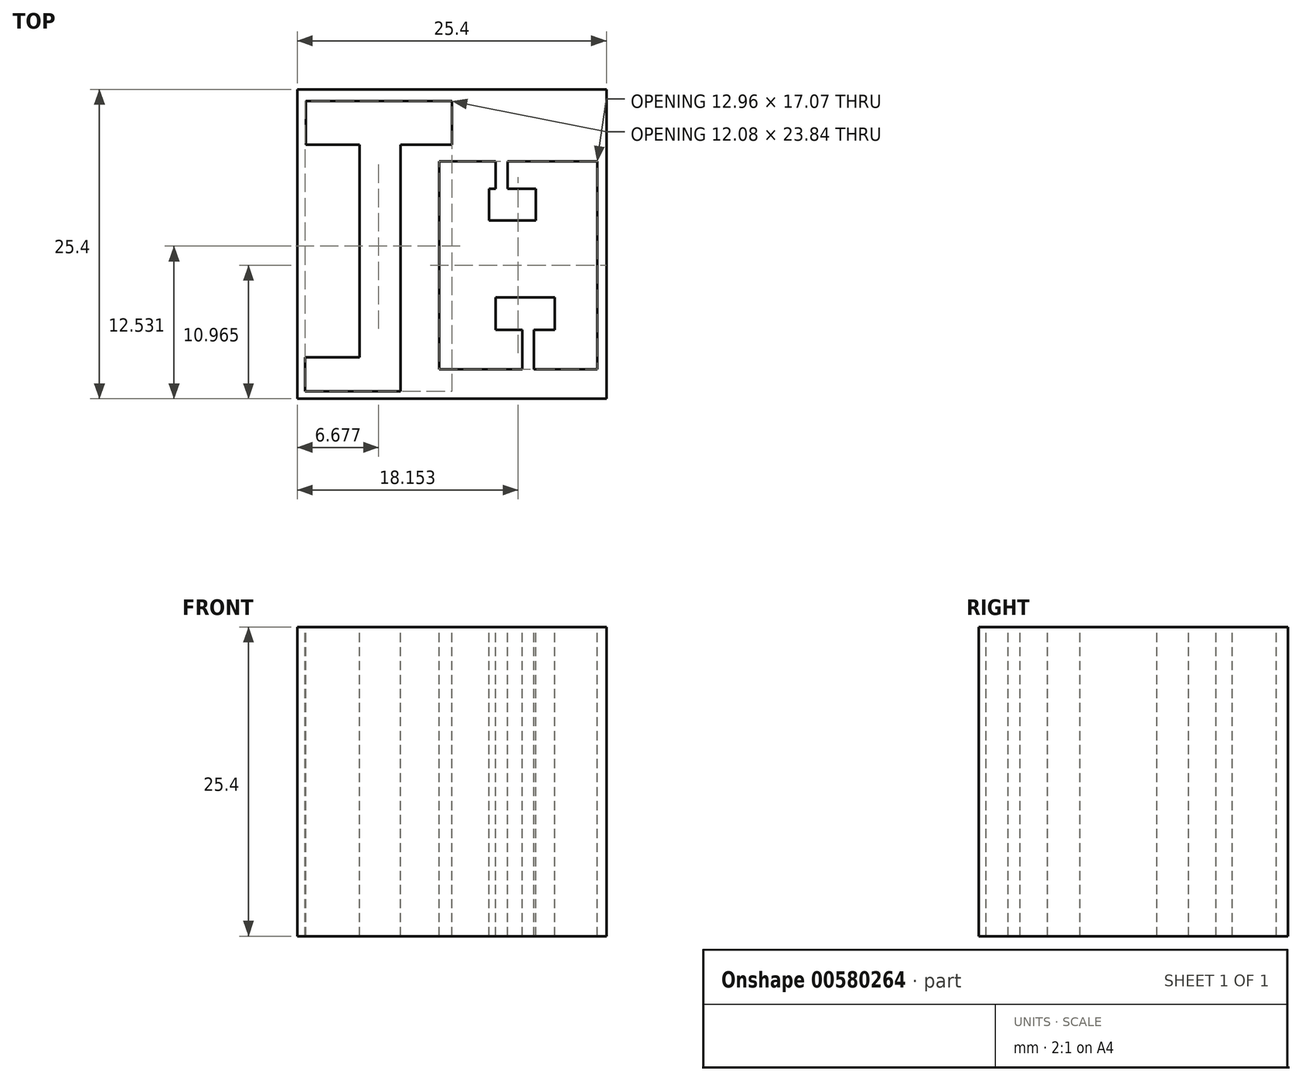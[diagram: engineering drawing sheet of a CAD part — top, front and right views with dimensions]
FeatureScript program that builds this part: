
annotation { "Feature Type Name" : "Feature", "Feature Type Description" : "" }
export const myFeature = defineFeature(function(context is Context, id is Id, definition is map)
    precondition{}
    {
        {
            var Q0;
            Q0=qCreatedBy(makeId("Top.planeOp"),FACE);
            var sketch = newSketch(context, id + "F0", { "sketchPlane" : qUnion([Q0])});
            skLineSegment(sketch, "E0.bottom", {"start": v(-13.3, 15.18) * mm, "end": v(12.1, 15.18) * mm});
            skLineSegment(sketch, "E0.top", {"start": v(-13.3, -10.22) * mm, "end": v(12.1, -10.22) * mm});
            skLineSegment(sketch, "E0.left", {"start": v(-13.3, 15.18) * mm, "end": v(-13.3, -10.22) * mm});
            skLineSegment(sketch, "E0.right", {"start": v(12.1, 15.18) * mm, "end": v(12.1, -10.22) * mm});
            skSolve(sketch);
        }
        {
            var Q0;
            Q0 = qSketchRegion(id + "F0", true);
            extrude(context, id + "F1", {"entities" : qUnion([Q0]), "depth" : 25.4 * mm, "offsetDistance" : 25.4 * mm});
        }
        {
            var Q0;
            Q0=makeQuery(id+"F1.opExtrude","CAP_FACE",FACE,{"disambiguationData":[OSD([sQuery(id+"F0.wireOp",EDGE,"E0.bottom"),sQuery(id+"F0.wireOp",EDGE,"E0.top"),sQuery(id+"F0.wireOp",EDGE,"E0.left"),sQuery(id+"F0.wireOp",EDGE,"E0.right")])],"isStart":false});
            var sketch = newSketch(context, id + "F2", { "sketchPlane" : qUnion([Q0])});
            skLineSegment(sketch, "E1.bottom", {"start": v(-12.6, 14.23) * mm, "end": v(-0.58, 14.23) * mm});
            skLineSegment(sketch, "E1.top", {"start": v(-12.6, 10.63) * mm, "end": v(-0.58, 10.63) * mm});
            skLineSegment(sketch, "E1.left", {"start": v(-12.6, 14.23) * mm, "end": v(-12.6, 10.63) * mm});
            skLineSegment(sketch, "E1.right", {"start": v(-0.58, 14.23) * mm, "end": v(-0.58, 10.63) * mm});
            skSolve(sketch);
        }
        {
            var Q0;
            Q0 = qSketchRegion(id + "F2", true);
            extrude(context, id + "F3", {"entities" : qUnion([Q0]), "operationType" : NewBodyOperationType.REMOVE, "endBound" : BoundingType.THROUGH_ALL, "oppositeDirection" : true, "depth" : 25.4 * mm, "offsetDistance" : 25.4 * mm});
        }
        {
            var Q0;
            Q0=makeQuery(id+"F1.opExtrude","CAP_FACE",FACE,{"disambiguationData":[OSD([sQuery(id+"F0.wireOp",EDGE,"E0.bottom"),sQuery(id+"F0.wireOp",EDGE,"E0.top"),sQuery(id+"F0.wireOp",EDGE,"E0.left"),sQuery(id+"F0.wireOp",EDGE,"E0.right")])],"isStart":false});
            var sketch = newSketch(context, id + "F4", { "sketchPlane" : qUnion([Q0])});
            skLineSegment(sketch, "E2.bottom", {"start": v(-8.17, 10.63) * mm, "end": v(-4.82, 10.63) * mm});
            skLineSegment(sketch, "E2.top", {"start": v(-8.17, -6.83) * mm, "end": v(-4.82, -6.83) * mm});
            skLineSegment(sketch, "E2.left", {"start": v(-8.17, 10.63) * mm, "end": v(-8.17, -6.83) * mm});
            skLineSegment(sketch, "E2.right", {"start": v(-4.82, 10.63) * mm, "end": v(-4.82, -6.83) * mm});
            skSolve(sketch);
        }
        {
            var Q0;
            Q0 = qSketchRegion(id + "F4", true);
            extrude(context, id + "F5", {"entities" : qUnion([Q0]), "operationType" : NewBodyOperationType.REMOVE, "endBound" : BoundingType.THROUGH_ALL, "oppositeDirection" : true, "depth" : 25.4 * mm, "offsetDistance" : 25.4 * mm});
        }
        {
            var Q0;
            Q0=makeQuery(id+"F1.opExtrude","CAP_FACE",FACE,{"disambiguationData":[OSD([sQuery(id+"F0.wireOp",EDGE,"E0.bottom"),sQuery(id+"F0.wireOp",EDGE,"E0.top"),sQuery(id+"F0.wireOp",EDGE,"E0.left"),sQuery(id+"F0.wireOp",EDGE,"E0.right")])],"isStart":false});
            var sketch = newSketch(context, id + "F6", { "sketchPlane" : qUnion([Q0])});
            skLineSegment(sketch, "E3.bottom", {"start": v(-4.82, -6.83) * mm, "end": v(-12.66, -6.83) * mm});
            skLineSegment(sketch, "E3.top", {"start": v(-4.82, -9.6) * mm, "end": v(-12.66, -9.6) * mm});
            skLineSegment(sketch, "E3.left", {"start": v(-4.82, -6.83) * mm, "end": v(-4.82, -9.6) * mm});
            skLineSegment(sketch, "E3.right", {"start": v(-12.66, -6.83) * mm, "end": v(-12.66, -9.6) * mm});
            skSolve(sketch);
        }
        {
            var Q0;
            Q0 = qSketchRegion(id + "F6", true);
            extrude(context, id + "F7", {"entities" : qUnion([Q0]), "operationType" : NewBodyOperationType.REMOVE, "endBound" : BoundingType.THROUGH_ALL, "oppositeDirection" : true, "depth" : 25.4 * mm, "offsetDistance" : 25.4 * mm});
        }
        {
            var Q0;
            Q0=makeQuery(id+"F1.opExtrude","CAP_FACE",FACE,{"disambiguationData":[OSD([sQuery(id+"F0.wireOp",EDGE,"E0.bottom"),sQuery(id+"F0.wireOp",EDGE,"E0.top"),sQuery(id+"F0.wireOp",EDGE,"E0.left"),sQuery(id+"F0.wireOp",EDGE,"E0.right")])],"isStart":false});
            var sketch = newSketch(context, id + "F8", { "sketchPlane" : qUnion([Q0])});
            skLineSegment(sketch, "E4.bottom", {"start": v(2.45, 7.02) * mm, "end": v(6.3, 7.02) * mm});
            skLineSegment(sketch, "E4.top", {"start": v(2.45, 4.43) * mm, "end": v(6.3, 4.43) * mm});
            skLineSegment(sketch, "E4.left", {"start": v(2.45, 7.02) * mm, "end": v(2.45, 4.43) * mm});
            skLineSegment(sketch, "E4.right", {"start": v(6.3, 7.02) * mm, "end": v(6.3, 4.43) * mm});
            skSolve(sketch);
        }
        {
            var Q0;
            Q0=makeQuery(id+"F8.imprint","IMPRINT",FACE,{"disambiguationData":[TD([[makeQuery(id+"F8.imprint","IMPRINT",EDGE,{"derivedFrom":sQuery(id+"F8.wireOp",EDGE,"E4.bottom")}),1.0]])]});
            var sketch = newSketch(context, id + "F9", { "sketchPlane" : qUnion([Q0])});
            skLineSegment(sketch, "E5.bottom", {"start": v(2.99, -1.91) * mm, "end": v(7.86, -1.91) * mm});
            skLineSegment(sketch, "E5.top", {"start": v(2.99, -4.57) * mm, "end": v(7.86, -4.57) * mm});
            skLineSegment(sketch, "E5.left", {"start": v(2.99, -1.91) * mm, "end": v(2.99, -4.57) * mm});
            skLineSegment(sketch, "E5.right", {"start": v(7.86, -1.91) * mm, "end": v(7.86, -4.57) * mm});
            skSolve(sketch);
        }
        {
            var Q0;
            Q0=makeQuery(id+"F8.imprint","IMPRINT",FACE,{"disambiguationData":[TD([[makeQuery(id+"F8.imprint","IMPRINT",EDGE,{"derivedFrom":sQuery(id+"F8.wireOp",EDGE,"E4.bottom")}),1.0]])]});
            var sketch = newSketch(context, id + "F10", { "sketchPlane" : qUnion([Q0])});
            skLineSegment(sketch, "E6.bottom", {"start": v(-1.63, 9.28) * mm, "end": v(11.33, 9.28) * mm});
            skLineSegment(sketch, "E6.top", {"start": v(-1.63, -7.8) * mm, "end": v(11.33, -7.8) * mm});
            skLineSegment(sketch, "E6.left", {"start": v(-1.63, 9.28) * mm, "end": v(-1.63, -7.8) * mm});
            skLineSegment(sketch, "E6.right", {"start": v(11.33, 9.28) * mm, "end": v(11.33, -7.8) * mm});
            skSolve(sketch);
        }
        {
            var Q0;
            Q0 = qSketchRegion(id + "F10", true);
            extrude(context, id + "F11", {"entities" : qUnion([Q0]), "operationType" : NewBodyOperationType.REMOVE, "endBound" : BoundingType.THROUGH_ALL, "oppositeDirection" : true, "depth" : 25.4 * mm, "offsetDistance" : 25.4 * mm});
        }
        {
            var Q0;
            Q0 = qSketchRegion(id + "F8", true);
            extrude(context, id + "F12", {"entities" : qUnion([Q0]), "operationType" : NewBodyOperationType.ADD, "oppositeDirection" : true, "depth" : 25.4 * mm, "offsetDistance" : 25.4 * mm});
        }
        {
            var Q0;
            Q0 = qSketchRegion(id + "F9", true);
            extrude(context, id + "F13", {"entities" : qUnion([Q0]), "operationType" : NewBodyOperationType.ADD, "oppositeDirection" : true, "depth" : 25.4 * mm, "offsetDistance" : 25.4 * mm});
        }
        {
            var Q0;
            Q0=qCreatedBy(makeId("Top.planeOp"),FACE);
            var sketch = newSketch(context, id + "F14", { "sketchPlane" : qUnion([Q0])});
            skLineSegment(sketch, "E7.bottom", {"start": v(-13.15, 14.65) * mm, "end": v(12.25, 14.65) * mm});
            skLineSegment(sketch, "E7.top", {"start": v(-13.15, -10.75) * mm, "end": v(12.25, -10.75) * mm});
            skLineSegment(sketch, "E7.left", {"start": v(-13.15, 14.65) * mm, "end": v(-13.15, -10.75) * mm});
            skLineSegment(sketch, "E7.right", {"start": v(12.25, 14.65) * mm, "end": v(12.25, -10.75) * mm});
            skSolve(sketch);
        }
        {
            var Q0;
            Q0=makeQuery(id+"F14.imprint","IMPRINT",FACE,{"disambiguationData":[TD([[makeQuery(id+"F14.imprint","IMPRINT",EDGE,{"derivedFrom":sQuery(id+"F14.wireOp",EDGE,"E7.bottom")}),-1.0]])]});
            var sketch = newSketch(context, id + "F15", { "sketchPlane" : qUnion([Q0])});
            skLineSegment(sketch, "E8.bottom", {"start": v(2.99, 9.87) * mm, "end": v(3.97, 9.87) * mm});
            skLineSegment(sketch, "E8.top", {"start": v(2.99, 6.38) * mm, "end": v(3.97, 6.38) * mm});
            skLineSegment(sketch, "E8.left", {"start": v(2.99, 9.87) * mm, "end": v(2.99, 6.38) * mm});
            skLineSegment(sketch, "E8.right", {"start": v(3.97, 9.87) * mm, "end": v(3.97, 6.38) * mm});
            skSolve(sketch);
        }
        {
            var Q0;
            Q0 = qSketchRegion(id + "F15", true);
            extrude(context, id + "F16", {"entities" : qUnion([Q0]), "operationType" : NewBodyOperationType.ADD, "depth" : 25.4 * mm, "offsetDistance" : 25.4 * mm});
        }
        {
            var Q0;
            Q0=makeQuery(id+"F14.imprint","IMPRINT",FACE,{"disambiguationData":[TD([[makeQuery(id+"F14.imprint","IMPRINT",EDGE,{"derivedFrom":sQuery(id+"F14.wireOp",EDGE,"E7.bottom")}),-1.0]])]});
            var sketch = newSketch(context, id + "F17", { "sketchPlane" : qUnion([Q0])});
            skLineSegment(sketch, "E9.bottom", {"start": v(5.2, -3.85) * mm, "end": v(6.16, -3.85) * mm});
            skLineSegment(sketch, "E9.top", {"start": v(5.2, -8.42) * mm, "end": v(6.16, -8.42) * mm});
            skLineSegment(sketch, "E9.left", {"start": v(5.2, -3.85) * mm, "end": v(5.2, -8.42) * mm});
            skLineSegment(sketch, "E9.right", {"start": v(6.16, -3.85) * mm, "end": v(6.16, -8.42) * mm});
            skSolve(sketch);
        }
        {
            var Q0;
            Q0 = qSketchRegion(id + "F17", true);
            extrude(context, id + "F18", {"entities" : qUnion([Q0]), "operationType" : NewBodyOperationType.ADD, "depth" : 25.4 * mm, "offsetDistance" : 25.4 * mm});
        }
    });
